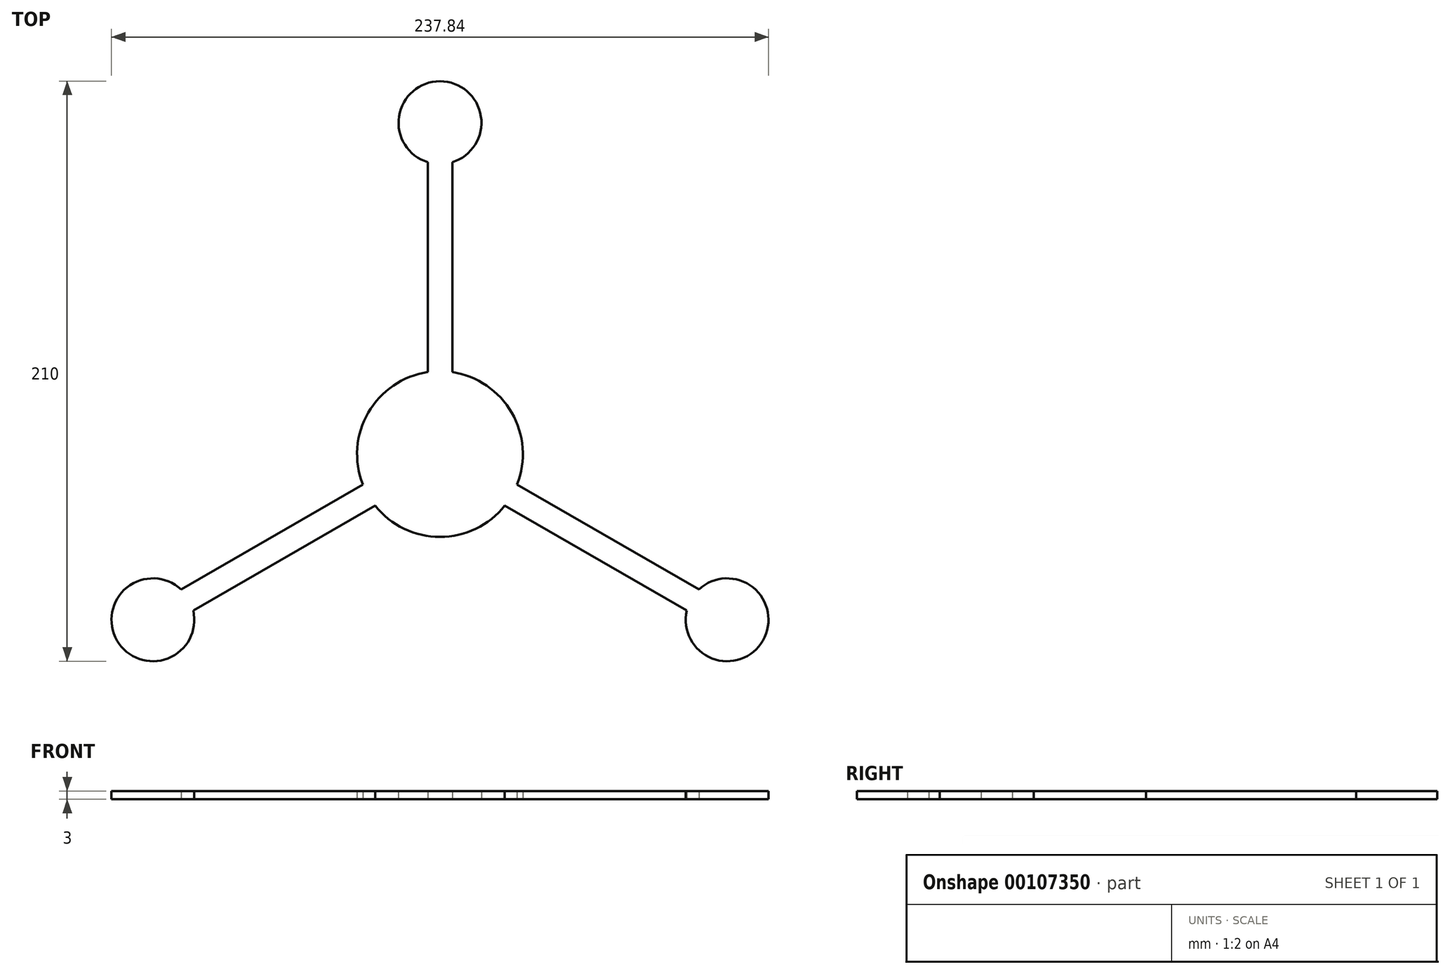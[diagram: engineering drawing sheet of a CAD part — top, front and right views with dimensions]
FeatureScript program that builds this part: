
annotation { "Feature Type Name" : "Feature", "Feature Type Description" : "" }
export const myFeature = defineFeature(function(context is Context, id is Id, definition is map)
    precondition{}
    {
        {
            var Q0;
            Q0=qCreatedBy(makeId("Top.planeOp"),FACE);
            var sketch = newSketch(context, id + "F0", { "sketchPlane" : qUnion([Q0])});
            skArc(sketch, "E0", {"start": v(4.43, 105.67) * mm, "mid": v(0, 135) * mm, "end": v(-4.43, 105.67) * mm});
            skArc(sketch, "E1", {"start": v(89.3, -56.68) * mm, "mid": v(116.91, -67.5) * mm, "end": v(93.73, -49) * mm});
            skArc(sketch, "E2", {"start": v(-93.73, -49) * mm, "mid": v(-116.91, -67.5) * mm, "end": v(-89.3, -56.68) * mm});
            skLineSegment(sketch, "E3", {"start": v(0, 0) * mm, "end": v(-103.92, -60) * mm, "construction": true});
            skLineSegment(sketch, "E4", {"start": v(0, 0) * mm, "end": v(103.92, -60) * mm, "construction": true});
            skLineSegment(sketch, "E5", {"start": v(0, 0) * mm, "end": v(0, 120) * mm, "construction": true});
            skArc(sketch, "E6", {"start": v(-4.43, 29.67) * mm, "mid": v(-25.98, 15) * mm, "end": v(-27.91, -11) * mm});
            skLineSegment(sketch, "E7", {"start": v(-4.43, 105.67) * mm, "end": v(-4.43, 29.67) * mm});
            skLineSegment(sketch, "E8", {"start": v(4.43, 105.67) * mm, "end": v(4.43, 29.67) * mm});
            skLineSegment(sketch, "E9", {"start": v(-93.73, -49) * mm, "end": v(-27.91, -11) * mm});
            skLineSegment(sketch, "E10", {"start": v(-89.3, -56.68) * mm, "end": v(-23.48, -18.68) * mm});
            skLineSegment(sketch, "E11", {"start": v(27.91, -11) * mm, "end": v(93.73, -49) * mm});
            skLineSegment(sketch, "E12", {"start": v(23.48, -18.68) * mm, "end": v(89.3, -56.68) * mm});
            skArc(sketch, "E13.trimOffspring", {"start": v(-23.48, -18.68) * mm, "mid": v(0, -30) * mm, "end": v(23.48, -18.68) * mm});
            skArc(sketch, "E14.trimOffspring", {"start": v(27.91, -11) * mm, "mid": v(25.98, 15) * mm, "end": v(4.43, 29.67) * mm});
            skSolve(sketch);
        }
        {
            var Q0;
            Q0 = qSketchRegion(id + "F0", true);
            extrude(context, id + "F1", {"entities" : qUnion([Q0]), "depth" : 3 * mm});
        }
    });
